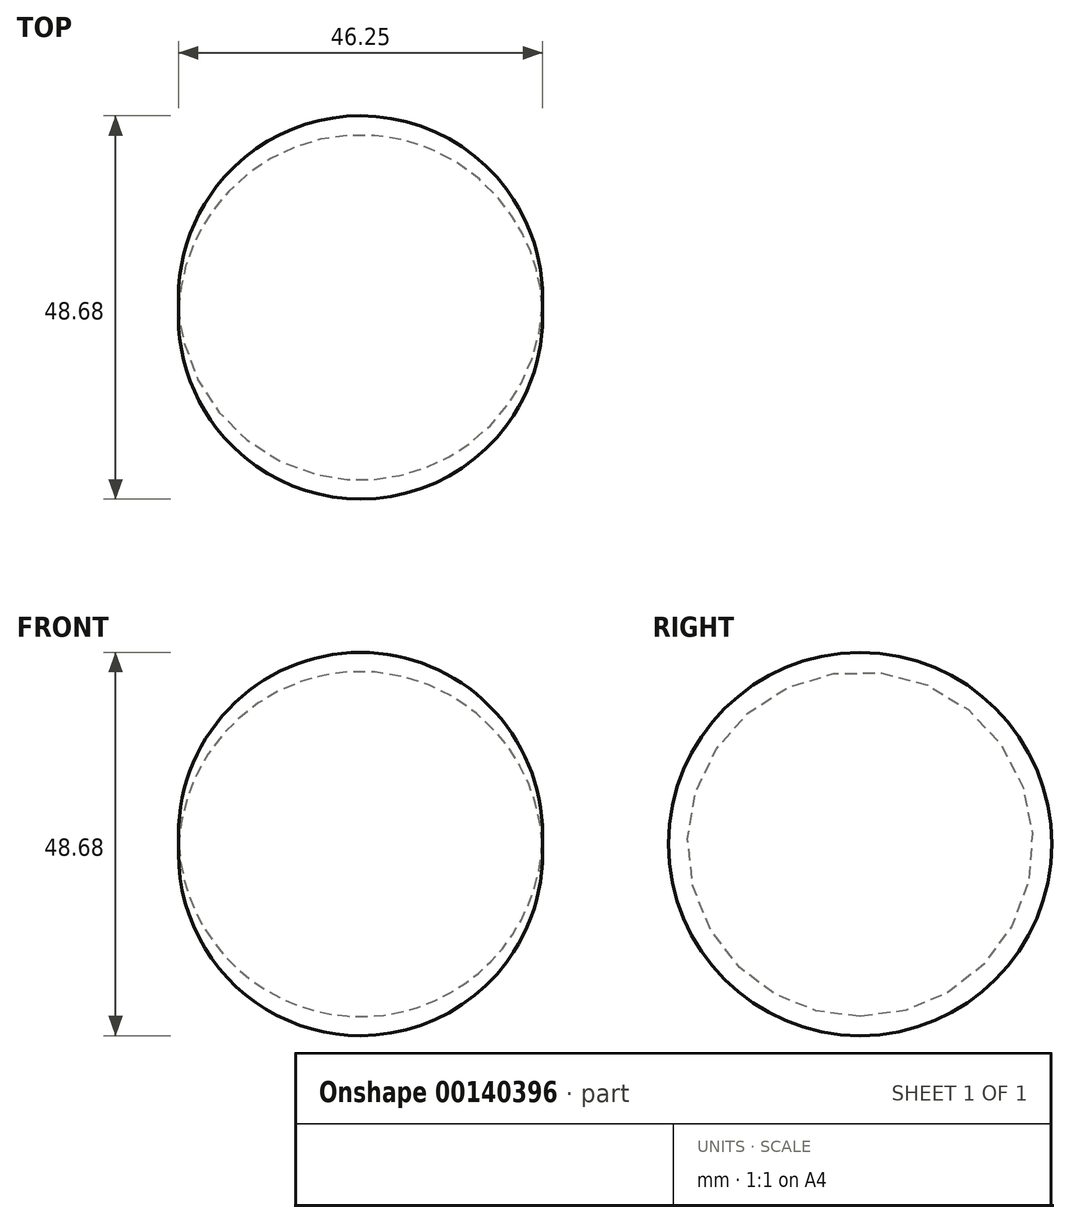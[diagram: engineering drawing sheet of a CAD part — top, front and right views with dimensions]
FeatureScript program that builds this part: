
annotation { "Feature Type Name" : "Feature", "Feature Type Description" : "" }
export const myFeature = defineFeature(function(context is Context, id is Id, definition is map)
    precondition{}
    {
        {
            var Q0;
            Q0=qCreatedBy(makeId("Front.planeOp"),FACE);
            var sketch = newSketch(context, id + "F0", { "sketchPlane" : qUnion([Q0])});
            skCircle(sketch, "E0", {"center": v(23.1, 1.21) * mm, "radius": 23.13 * mm});
            skPoint(sketch, "E0.first.point", {"position": v(0, 0) * mm});
            skPoint(sketch, "E0.second.point", {"position": v(46.19, 0) * mm});
            skPoint(sketch, "E0.third.point", {"position": v(23.84, -21.9) * mm});
            skLineSegment(sketch, "E1", {"start": v(0, 0) * mm, "end": v(46.19, 0) * mm});
            skSolve(sketch);
        }
        {
            var Q0;
            {var subQ0=sQuery(id+"F0.wireOp",EDGE,"E1");Q0=makeQuery(id+"F0.imprint","IMPRINT",FACE,{"disambiguationData":[TD([[makeQuery(id+"F0.imprint","IMPRINT",EDGE,{"derivedFrom":subQ0}),1.0]])]});}
            var Q1;
            Q1=sQuery(id+"F0.wireOp",EDGE,"E1");
            revolve(context, id + "F1", {"entities" : qUnion([Q0]), "axis" : qUnion([Q1]), "revolveType" : RevolveType.FULL});
        }
    });
